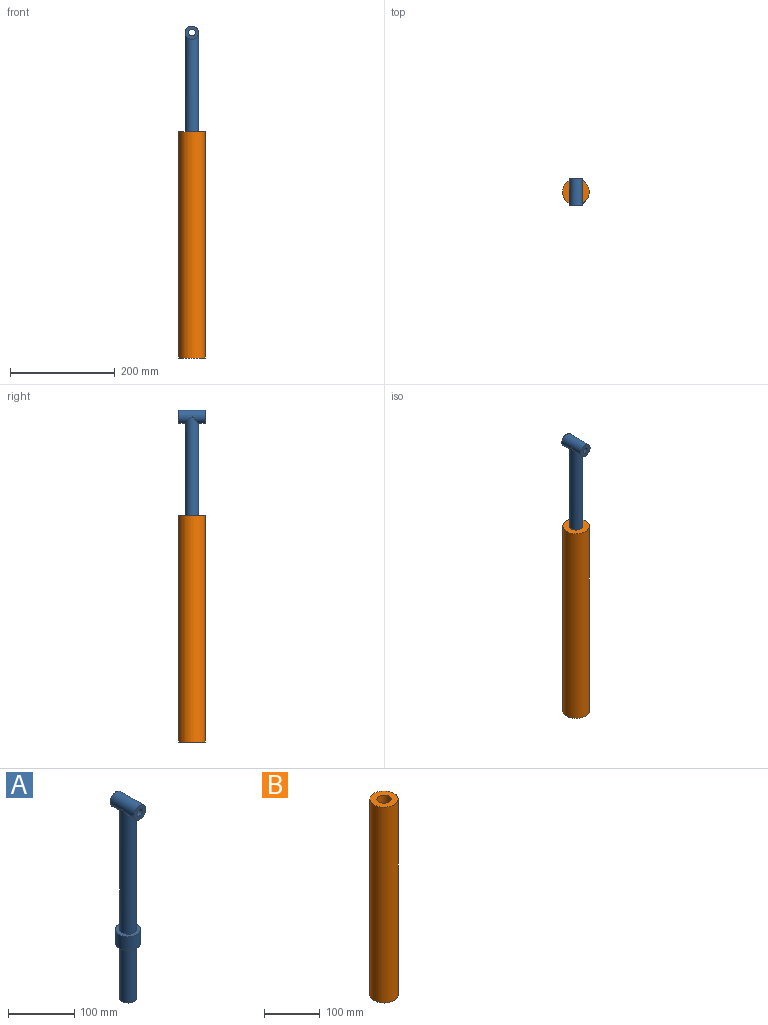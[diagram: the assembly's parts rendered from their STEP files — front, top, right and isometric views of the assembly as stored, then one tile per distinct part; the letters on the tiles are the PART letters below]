
ASSEMBLY  parts=2 mates=1
PART A: 10 faces, bbox 38.1x50.8x368.3 mm
  f0: cylinder r=12.7mm len=228.6mm, axis (0,0,1), area 17596.3mm2, adj f5,f6
  f1: cylinder r=12.7mm len=101.6mm, axis (0,0,1), area 8107.3mm2, adj f2,f4
  f2: plane 25.4x25.4mm, normal (0,0,-1), area 506.7mm2, adj f1
  f3: cylinder r=19.05mm len=38.1mm, axis (0,0,1), area 3040.2mm2, adj f4,f5
  f4: plane 38.1x38.1mm, normal (0,0,-1), area 633.4mm2, adj f1,f3
  f5: plane 38.1x38.1mm, normal (0,0,1), area 633.4mm2, adj f0,f3
  f6: cylinder r=12.7mm len=50.8mm, axis (0,1,0), area 3408.5mm2, adj f0,f7,f8
  f7: plane 25.4x25.4mm, normal (0,-1,0), area 380mm2, adj f6,f9
  f8: plane 25.4x25.4mm, normal (0,1,0), area 380mm2, adj f6,f9
  f9: cylinder r=6.35mm len=50.8mm, axis (0,-1,0), area 2026.8mm2, adj f7,f8
PART B: 7 faces, bbox 50.8x50.8x431.8 mm
  f0: cylinder r=25.4mm len=431.8mm, axis (0,0,1), area 68912.2mm2, adj f1,f2
  f1: plane 50.8x50.8mm, normal (0,0,-1), area 2026.8mm2, adj f0
  f2: plane 50.8x50.8mm, normal (0,0,1), area 1520.1mm2, adj f0,f3
  f3: cylinder r=12.7mm len=25.4mm, axis (0,0,-1), area 2026.8mm2, adj f2,f6
  f4: cylinder r=19.05mm len=355.6mm, axis (0,0,1), area 42563.4mm2, adj f5,f6
  f5: plane 38.1x38.1mm, normal (0,0,1), area 1140.1mm2, adj f4
  f6: plane 38.1x38.1mm, normal (0,0,-1), area 633.4mm2, adj f3,f4
PLACE A t=(0,0,380.31)mm
PLACE B t=(0,0,190.5)mm
MATE slider A.f0 <-> B.f0  axis (0,0,1) through (0,0,292.1)mm
